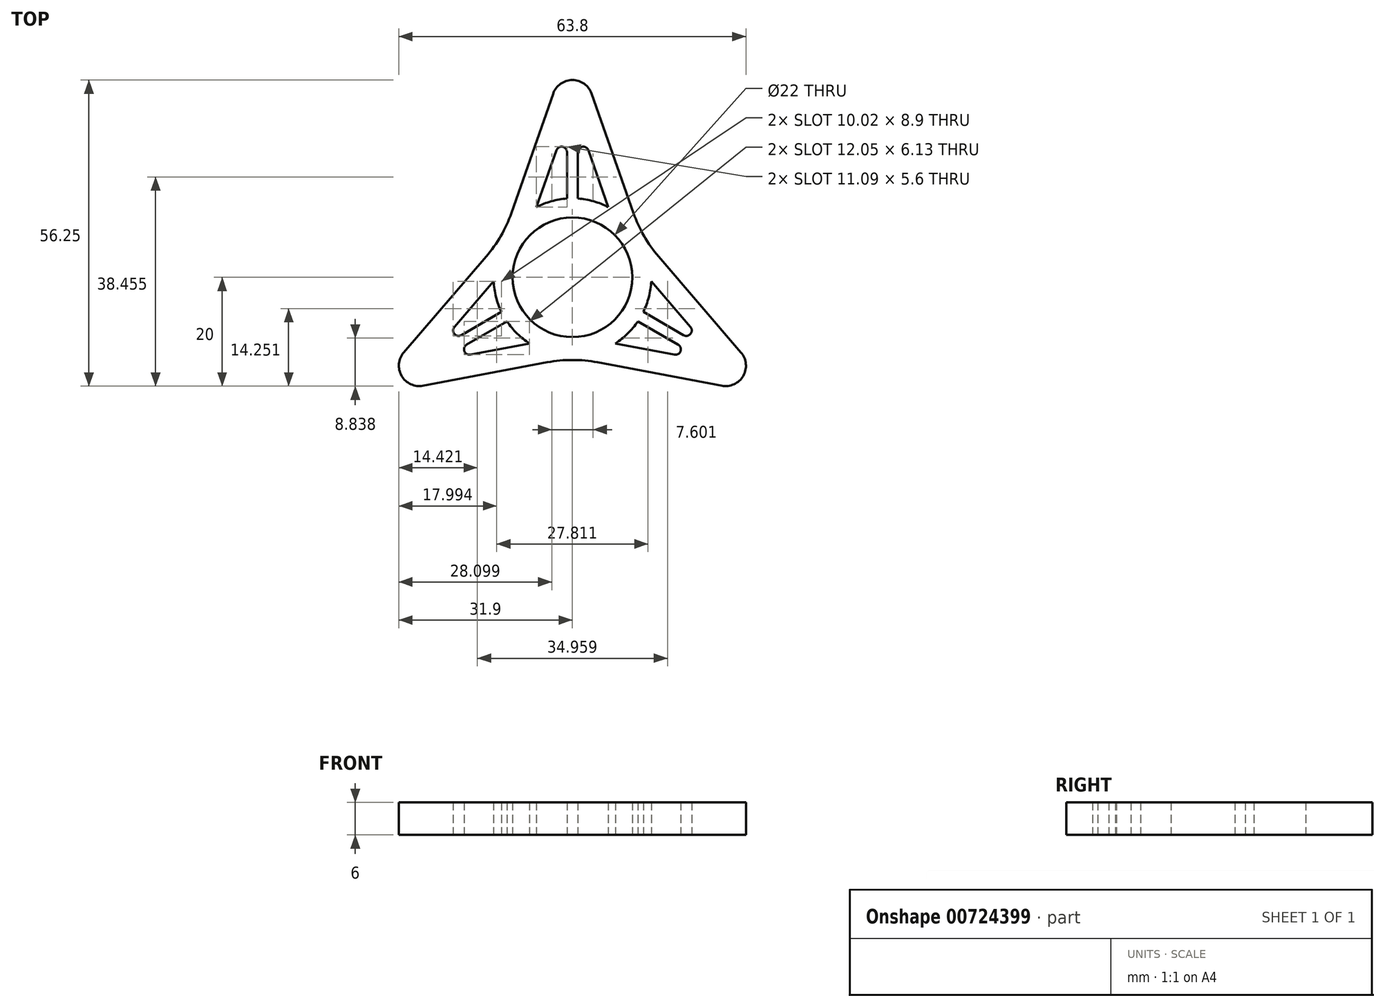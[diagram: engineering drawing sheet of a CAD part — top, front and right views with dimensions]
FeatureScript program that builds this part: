
annotation { "Feature Type Name" : "Feature", "Feature Type Description" : "" }
export const myFeature = defineFeature(function(context is Context, id is Id, definition is map)
    precondition{}
    {
        {
            var Q0;
            Q0=qCreatedBy(makeId("Top.planeOp"),FACE);
            var sketch = newSketch(context, id + "F0", { "sketchPlane" : qUnion([Q0])});
            skCircle(sketch, "E0", {"center": v(0, 0) * mm, "radius": 11 * mm});
            skArc(sketch, "E1", {"start": v(-12.03, -8.1) * mm, "mid": v(-10.16, -10.35) * mm, "end": v(-7.88, -12.17) * mm});
            skLineSegment(sketch, "E2", {"start": v(0, 40.81) * mm, "end": v(0, -43.66) * mm, "construction": true});
            skLineSegment(sketch, "E3", {"start": v(54.3, -31.35) * mm, "end": v(-41.87, 24.17) * mm, "construction": true});
            skLineSegment(sketch, "E4", {"start": v(-54.3, -31.35) * mm, "end": v(45.05, 26.01) * mm, "construction": true});
            skArc(sketch, "E5", {"start": v(3.54, 33.74) * mm, "mid": v(0, 36.25) * mm, "end": v(-3.54, 33.74) * mm});
            skCircle(sketch, "E6.1.0", {"center": v(-28.15, -16.25) * mm, "radius": 3.75 * mm});
            skCircle(sketch, "E6.2.0", {"center": v(28.15, -16.25) * mm, "radius": 3.75 * mm});
            skPoint(sketch, "E7", {"position": v(0, 36.25) * mm});
            skLineSegment(sketch, "E8", {"start": v(3.54, 33.74) * mm, "end": v(12.78, 7.38) * mm, "construction": true});
            skLineSegment(sketch, "E9", {"start": v(2.94, 23.35) * mm, "end": v(6.6, 12.91) * mm});
            skArc(sketch, "E10", {"start": v(1.13, 28.92) * mm, "mid": v(0.94, 28.98) * mm, "end": v(0.75, 29.02) * mm});
            skLineSegment(sketch, "E11.MirrorCS", {"start": v(-2.94, 23.35) * mm, "end": v(-6.6, 12.91) * mm});
            skLineSegment(sketch, "E12.MirrorCS", {"start": v(-3.54, 33.74) * mm, "end": v(-11.22, 11.83) * mm});
            skLineSegment(sketch, "E13.MirrorCS", {"start": v(30.99, -13.8) * mm, "end": v(12.78, 7.38) * mm, "construction": true});
            skLineSegment(sketch, "E14.MirrorCS", {"start": v(21.69, -9.12) * mm, "end": v(14.48, -0.74) * mm});
            skLineSegment(sketch, "E15.MirrorCS", {"start": v(-30.99, -13.8) * mm, "end": v(-15.85, 3.8) * mm});
            skLineSegment(sketch, "E16.MirrorCS", {"start": v(-21.69, -9.12) * mm, "end": v(-14.48, -0.74) * mm});
            skLineSegment(sketch, "E17.MirrorCS", {"start": v(-18.75, -14.22) * mm, "end": v(-7.88, -12.17) * mm});
            skLineSegment(sketch, "E18.MirrorCS", {"start": v(-27.45, -19.93) * mm, "end": v(0, -14.76) * mm, "construction": true});
            skLineSegment(sketch, "E19.MirrorCS", {"start": v(18.75, -14.22) * mm, "end": v(7.88, -12.17) * mm});
            skLineSegment(sketch, "E20.MirrorCS", {"start": v(27.45, -19.93) * mm, "end": v(0, -14.76) * mm, "construction": true});
            skArc(sketch, "E21.trimOffspring", {"start": v(-3.02, 23.13) * mm, "mid": v(0, 21.6) * mm, "end": v(3.02, 23.13) * mm, "construction": true});
            skArc(sketch, "E22.trimOffspring", {"start": v(-1.13, 28.92) * mm, "mid": v(0, 28.75) * mm, "end": v(1.13, 28.92) * mm, "construction": true});
            skArc(sketch, "E23.MirrorCS", {"start": v(-24.48, -15.44) * mm, "mid": v(-24.63, -15.3) * mm, "end": v(-24.76, -15.16) * mm});
            skArc(sketch, "E24.MirrorCS", {"start": v(-21.54, -8.95) * mm, "mid": v(-18.7, -10.8) * mm, "end": v(-18.52, -14.18) * mm, "construction": true});
            skArc(sketch, "E25.MirrorCS", {"start": v(25.61, -13.48) * mm, "mid": v(25.57, -13.67) * mm, "end": v(25.5, -13.86) * mm});
            skArc(sketch, "E26.MirrorCS", {"start": v(18.52, -14.18) * mm, "mid": v(18.7, -10.8) * mm, "end": v(21.54, -8.95) * mm, "construction": true});
            skLineSegment(sketch, "E27", {"start": v(-1, 23.01) * mm, "end": v(-1, 14.47) * mm});
            skLineSegment(sketch, "E28.MirrorCS", {"start": v(1, 23.01) * mm, "end": v(1, 14.47) * mm});
            skLineSegment(sketch, "E29.MirrorCS", {"start": v(20.43, -10.64) * mm, "end": v(13.03, -6.37) * mm});
            skLineSegment(sketch, "E30.MirrorCS", {"start": v(19.43, -12.37) * mm, "end": v(12.03, -8.1) * mm});
            skLineSegment(sketch, "E31.MirrorCS", {"start": v(-20.43, -10.64) * mm, "end": v(-13.03, -6.37) * mm});
            skLineSegment(sketch, "E32.MirrorCS", {"start": v(-19.43, -12.37) * mm, "end": v(-12.03, -8.1) * mm});
            skArc(sketch, "E33.trimOffspring", {"start": v(-25.5, -13.86) * mm, "mid": v(-25.57, -13.67) * mm, "end": v(-25.61, -13.48) * mm});
            skArc(sketch, "E34.trimOffspring", {"start": v(24.76, -15.16) * mm, "mid": v(24.63, -15.3) * mm, "end": v(24.48, -15.44) * mm});
            skArc(sketch, "E35.trimOffspring", {"start": v(13.03, -6.37) * mm, "mid": v(14.04, -3.63) * mm, "end": v(14.48, -0.74) * mm});
            skArc(sketch, "E36.trimOffspring", {"start": v(-1, 14.47) * mm, "mid": v(-3.88, 13.97) * mm, "end": v(-6.6, 12.91) * mm});
            skArc(sketch, "E37.trimOffspring", {"start": v(-0.75, 29.02) * mm, "mid": v(-0.94, 28.98) * mm, "end": v(-1.13, 28.92) * mm});
            skArc(sketch, "E38.trimOffspring", {"start": v(-14.48, -0.74) * mm, "mid": v(-14.04, -3.63) * mm, "end": v(-13.03, -6.37) * mm});
            skPoint(sketch, "E39.orphan", {"position": v(-11, 9.45) * mm});
            skPoint(sketch, "E40.orphan", {"position": v(-13.68, 4.8) * mm});
            skArc(sketch, "E41.trimOffspring", {"start": v(7.88, -12.17) * mm, "mid": v(10.16, -10.35) * mm, "end": v(12.03, -8.1) * mm});
            skPoint(sketch, "E42.orphan", {"position": v(2.69, -14.25) * mm});
            skPoint(sketch, "E43.orphan", {"position": v(-2.69, -14.25) * mm});
            skArc(sketch, "E44.trimOffspring", {"start": v(6.6, 12.91) * mm, "mid": v(3.88, 13.97) * mm, "end": v(1, 14.47) * mm});
            skPoint(sketch, "E45.orphan", {"position": v(11, 9.45) * mm});
            skPoint(sketch, "E46.orphan", {"position": v(13.68, 4.8) * mm});
            skPoint(sketch, "E47.newPointA", {"position": v(1, 26.02) * mm});
            skPoint(sketch, "E47.newPointB", {"position": v(2.11, 25.72) * mm});
            skArc(sketch, "E47.filletArc", {"start": v(2.94, 23.35) * mm, "mid": v(1.83, 24) * mm, "end": v(1, 23.01) * mm});
            skPoint(sketch, "E48.newPointA", {"position": v(-2.11, 25.72) * mm});
            skPoint(sketch, "E48.newPointB", {"position": v(-1, 26.02) * mm});
            skArc(sketch, "E48.filletArc", {"start": v(-1, 23.01) * mm, "mid": v(-1.83, 24) * mm, "end": v(-2.94, 23.35) * mm});
            skPoint(sketch, "E49.newPointA", {"position": v(-23.33, -11.03) * mm});
            skPoint(sketch, "E49.newPointB", {"position": v(-23.04, -12.15) * mm});
            skArc(sketch, "E49.filletArc", {"start": v(-21.69, -9.12) * mm, "mid": v(-21.7, -10.41) * mm, "end": v(-20.43, -10.64) * mm});
            skPoint(sketch, "E50.newPointA", {"position": v(-21.22, -14.69) * mm});
            skPoint(sketch, "E50.newPointB", {"position": v(-22.04, -13.88) * mm});
            skArc(sketch, "E50.filletArc", {"start": v(-19.43, -12.37) * mm, "mid": v(-19.87, -13.59) * mm, "end": v(-18.75, -14.22) * mm});
            skPoint(sketch, "E51.newPointA", {"position": v(21.22, -14.69) * mm});
            skPoint(sketch, "E51.newPointB", {"position": v(22.04, -13.88) * mm});
            skArc(sketch, "E51.filletArc", {"start": v(18.75, -14.22) * mm, "mid": v(19.87, -13.59) * mm, "end": v(19.43, -12.37) * mm});
            skPoint(sketch, "E52.newPointA", {"position": v(23.04, -12.15) * mm});
            skPoint(sketch, "E52.newPointB", {"position": v(23.33, -11.03) * mm});
            skArc(sketch, "E52.filletArc", {"start": v(20.43, -10.64) * mm, "mid": v(21.7, -10.41) * mm, "end": v(21.69, -9.12) * mm});
            skPoint(sketch, "E53.visualSharp", {"position": v(-12.78, 7.38) * mm});
            skArc(sketch, "E53.filletArc", {"start": v(-15.85, 3.8) * mm, "mid": v(-13.16, 7.6) * mm, "end": v(-11.22, 11.83) * mm});
            skArc(sketch, "E54.1.0", {"start": v(4.64, -15.63) * mm, "mid": v(0, -15.2) * mm, "end": v(-4.64, -15.63) * mm});
            skArc(sketch, "E54.2.0", {"start": v(11.22, 11.83) * mm, "mid": v(13.16, 7.6) * mm, "end": v(15.85, 3.8) * mm});
            skLineSegment(sketch, "E55", {"start": v(3.54, 33.74) * mm, "end": v(11.22, 11.83) * mm});
            skLineSegment(sketch, "E56", {"start": v(15.85, 3.8) * mm, "end": v(30.99, -13.8) * mm});
            skLineSegment(sketch, "E57", {"start": v(27.45, -19.93) * mm, "end": v(4.64, -15.63) * mm});
            skLineSegment(sketch, "E58", {"start": v(-4.64, -15.63) * mm, "end": v(-27.45, -19.93) * mm});
            skSolve(sketch);
        }
        {
            var Q0;
            Q0=makeQuery(id+"F0.imprint","IMPRINT",FACE,{"disambiguationData":[TD([[makeQuery(id+"F0.imprint","IMPRINT",EDGE,{"derivedFrom":sQuery(id+"F0.wireOp",EDGE,"E0")}),-1.0]])]});
            var Q1;
            {var subQ5=sQuery(id+"F0.wireOp",EDGE,"E23.MirrorCS");Q1=makeQuery(id+"F0.imprint","IMPRINT",FACE,{"disambiguationData":[TD([[makeQuery(id+"F0.imprint","IMPRINT",EDGE,{"derivedFrom":subQ5}),1.0]])]});}
            var Q2;
            {var subQ7=sQuery(id+"F0.wireOp",EDGE,"E25.MirrorCS");Q2=makeQuery(id+"F0.imprint","IMPRINT",FACE,{"disambiguationData":[TD([[makeQuery(id+"F0.imprint","IMPRINT",EDGE,{"derivedFrom":subQ7}),1.0]])]});}
            var Q3;
            {var subQ0=sQuery(id+"F0.wireOp",EDGE,"E6.1.0");var subQ3=makeQuery(id+"F0.imprint","IMPRINT",VERTEX,{"disambiguationData":[OD(0.0)],"derivedFrom":subQ0});Q3=makeQuery(id+"F0.imprint","IMPRINT",FACE,{"disambiguationData":[TD([[makeQuery(id+"F0.imprint","IMPRINT",EDGE,{"disambiguationData":[TD([[subQ3,-1.0]])],"derivedFrom":subQ0}),1.0]])]});}
            var Q4;
            {var subQ0=sQuery(id+"F0.wireOp",EDGE,"E6.2.0");var subQ3=makeQuery(id+"F0.imprint","IMPRINT",VERTEX,{"disambiguationData":[OD(0.0)],"derivedFrom":subQ0});Q4=makeQuery(id+"F0.imprint","IMPRINT",FACE,{"disambiguationData":[TD([[makeQuery(id+"F0.imprint","IMPRINT",EDGE,{"disambiguationData":[TD([[subQ3,-1.0]])],"derivedFrom":subQ0}),1.0]])]});}
            extrude(context, id + "F1", {"entities" : qUnion([Q0, Q1, Q2, Q3, Q4]), "depth" : 6 * mm, "offsetDistance" : 25 * mm});
        }
    });
